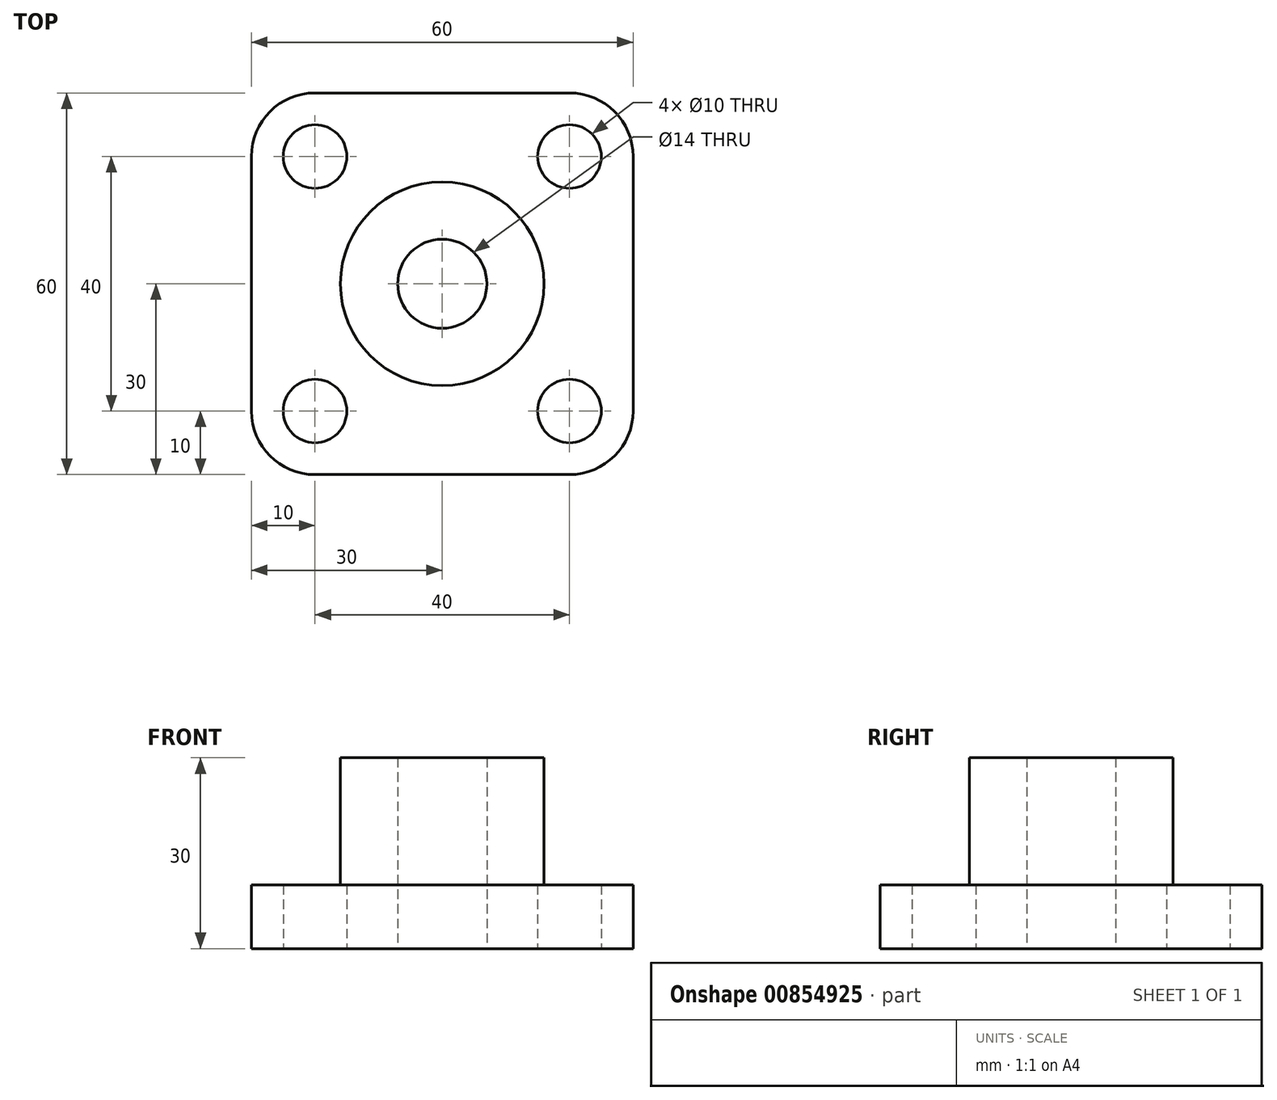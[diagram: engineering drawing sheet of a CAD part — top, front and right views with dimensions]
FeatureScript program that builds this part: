
annotation { "Feature Type Name" : "Feature", "Feature Type Description" : "" }
export const myFeature = defineFeature(function(context is Context, id is Id, definition is map)
    precondition{}
    {
        {
            var Q0;
            Q0=qCreatedBy(makeId("Front.planeOp"),FACE);
            var sketch = newSketch(context, id + "F0", { "sketchPlane" : qUnion([Q0])});
            skCircle(sketch, "E0", {"center": v(0, 0) * mm, "radius": 16 * mm});
            skLineSegment(sketch, "E1", {"start": v(0, 0) * mm, "end": v(-20, 0) * mm});
            skLineSegment(sketch, "E2", {"start": v(0, 0) * mm, "end": v(20, 0) * mm});
            skLineSegment(sketch, "E3", {"start": v(-20, 0) * mm, "end": v(-20, -20) * mm});
            skLineSegment(sketch, "E4", {"start": v(-20, 0) * mm, "end": v(-20, 20) * mm});
            skLineSegment(sketch, "E5", {"start": v(20, 0) * mm, "end": v(20, -20) * mm});
            skLineSegment(sketch, "E6", {"start": v(20, 0) * mm, "end": v(20, 20) * mm});
            skCircle(sketch, "E7", {"center": v(-20, 20) * mm, "radius": 5 * mm});
            skCircle(sketch, "E8", {"center": v(-20, -20) * mm, "radius": 5 * mm});
            skCircle(sketch, "E9", {"center": v(20, -20) * mm, "radius": 5 * mm});
            skCircle(sketch, "E10", {"center": v(20, 20) * mm, "radius": 5 * mm});
            skArc(sketch, "E11", {"start": v(-20, 30) * mm, "mid": v(-27.07, 27.07) * mm, "end": v(-30, 20) * mm});
            skArc(sketch, "E12", {"start": v(30, 20) * mm, "mid": v(27.07, 27.07) * mm, "end": v(20, 30) * mm});
            skArc(sketch, "E13", {"start": v(20, -30) * mm, "mid": v(27.07, -27.07) * mm, "end": v(30, -20) * mm});
            skArc(sketch, "E14", {"start": v(-30, -20) * mm, "mid": v(-27.07, -27.07) * mm, "end": v(-20, -30) * mm});
            skLineSegment(sketch, "E15", {"start": v(-20, -30) * mm, "end": v(20, -30) * mm});
            skLineSegment(sketch, "E16", {"start": v(30, 20) * mm, "end": v(30, -20) * mm});
            skLineSegment(sketch, "E17", {"start": v(-20, 30) * mm, "end": v(20, 30) * mm});
            skLineSegment(sketch, "E18", {"start": v(-30, 20) * mm, "end": v(-30, -20) * mm});
            skSolve(sketch);
        }
        {
            var Q0;
            {var subQ0=sQuery(id+"F0.wireOp",EDGE,"E18");Q0=makeQuery(id+"F0.imprint","IMPRINT",FACE,{"disambiguationData":[TD([[makeQuery(id+"F0.imprint","IMPRINT",EDGE,{"derivedFrom":subQ0}),1.0]])]});}
            var Q1;
            {var subQ5=sQuery(id+"F0.wireOp",EDGE,"E17");Q1=makeQuery(id+"F0.imprint","IMPRINT",FACE,{"disambiguationData":[TD([[makeQuery(id+"F0.imprint","IMPRINT",EDGE,{"derivedFrom":subQ5}),-1.0]])]});}
            var Q2;
            Q2=makeQuery(id+"F0.imprint","IMPRINT",FACE,{"disambiguationData":[TD([[makeQuery(id+"F0.imprint","IMPRINT",EDGE,{"derivedFrom":sQuery(id+"F0.wireOp",EDGE,"E7")}),-1.0]])]});
            var Q3;
            Q3=makeQuery(id+"F0.imprint","IMPRINT",FACE,{"disambiguationData":[TD([[makeQuery(id+"F0.imprint","IMPRINT",EDGE,{"derivedFrom":sQuery(id+"F0.wireOp",EDGE,"E10")}),-1.0]])]});
            var Q4;
            {var subQ0=sQuery(id+"F0.wireOp",EDGE,"E16");Q4=makeQuery(id+"F0.imprint","IMPRINT",FACE,{"disambiguationData":[TD([[makeQuery(id+"F0.imprint","IMPRINT",EDGE,{"derivedFrom":subQ0}),-1.0]])]});}
            var Q5;
            {var subQ9=sQuery(id+"F0.wireOp",EDGE,"E15");Q5=makeQuery(id+"F0.imprint","IMPRINT",FACE,{"disambiguationData":[TD([[makeQuery(id+"F0.imprint","IMPRINT",EDGE,{"derivedFrom":subQ9}),1.0]])]});}
            var Q6;
            Q6=makeQuery(id+"F0.imprint","IMPRINT",FACE,{"disambiguationData":[TD([[makeQuery(id+"F0.imprint","IMPRINT",EDGE,{"derivedFrom":sQuery(id+"F0.wireOp",EDGE,"E9")}),-1.0]])]});
            var Q7;
            Q7=makeQuery(id+"F0.imprint","IMPRINT",FACE,{"disambiguationData":[TD([[makeQuery(id+"F0.imprint","IMPRINT",EDGE,{"derivedFrom":sQuery(id+"F0.wireOp",EDGE,"E8")}),-1.0]])]});
            var Q8;
            {var subQ0=sQuery(id+"F0.wireOp",EDGE,"E1");var subQ1=sQuery(id+"F0.wireOp",EDGE,"E0");var subQ2=makeQuery(id+"F0.imprint","INTERSECT",VERTEX,{"derivedFrom":[subQ1,subQ0]});Q8=makeQuery(id+"F0.imprint","IMPRINT",FACE,{"disambiguationData":[TD([[makeQuery(id+"F0.imprint","IMPRINT",EDGE,{"disambiguationData":[TD([[subQ2,-1.0]])],"derivedFrom":subQ1}),1.0]])]});}
            var Q9;
            {var subQ0=sQuery(id+"F0.wireOp",EDGE,"E1");var subQ1=sQuery(id+"F0.wireOp",EDGE,"E0");var subQ2=makeQuery(id+"F0.imprint","INTERSECT",VERTEX,{"derivedFrom":[subQ1,subQ0]});Q9=makeQuery(id+"F0.imprint","IMPRINT",FACE,{"disambiguationData":[TD([[makeQuery(id+"F0.imprint","IMPRINT",EDGE,{"disambiguationData":[TD([[subQ2,1.0]])],"derivedFrom":subQ1}),1.0]])]});}
            extrude(context, id + "F1", {"entities" : qUnion([Q0, Q1, Q2, Q3, Q4, Q5, Q6, Q7, Q8, Q9]), "depth" : 10 * mm, "offsetDistance" : 25 * mm});
        }
        {
            var Q0;
            Q0=makeQuery(id+"F1.opExtrude","CAP_FACE",FACE,{"disambiguationData":[OSD([sQuery(id+"F0.wireOp",EDGE,"E7"),sQuery(id+"F0.wireOp",EDGE,"E8"),sQuery(id+"F0.wireOp",EDGE,"E9"),sQuery(id+"F0.wireOp",EDGE,"E10"),sQuery(id+"F0.wireOp",EDGE,"E11"),sQuery(id+"F0.wireOp",EDGE,"E12"),sQuery(id+"F0.wireOp",EDGE,"E13"),sQuery(id+"F0.wireOp",EDGE,"E14"),sQuery(id+"F0.wireOp",EDGE,"E15"),sQuery(id+"F0.wireOp",EDGE,"E16"),sQuery(id+"F0.wireOp",EDGE,"E17"),sQuery(id+"F0.wireOp",EDGE,"E18")])],"isStart":false});
            var sketch = newSketch(context, id + "F2", { "sketchPlane" : qUnion([Q0])});
            skCircle(sketch, "E19", {"center": v(0, 0) * mm, "radius": 16 * mm});
            skSolve(sketch);
        }
        {
            var Q0;
            Q0=makeQuery(id+"F2.imprint","IMPRINT",FACE,{"disambiguationData":[TD([[makeQuery(id+"F2.imprint","IMPRINT",EDGE,{"derivedFrom":sQuery(id+"F2.wireOp",EDGE,"E19")}),1.0]])]});
            extrude(context, id + "F3", {"entities" : qUnion([Q0]), "operationType" : NewBodyOperationType.ADD, "depth" : 20 * mm, "offsetDistance" : 25 * mm});
        }
        {
            var Q0;
            Q0=sQuery(id+"F0.wireOp",VERTEX,"E1.start");
            var Q1;
            Q1=makeQuery(id+"F1.opExtrude","SWEPT_BODY",BODY,{"disambiguationData":[OSD([sQuery(id+"F0.wireOp",EDGE,"E7"),sQuery(id+"F0.wireOp",EDGE,"E8"),sQuery(id+"F0.wireOp",EDGE,"E9"),sQuery(id+"F0.wireOp",EDGE,"E10"),sQuery(id+"F0.wireOp",EDGE,"E11"),sQuery(id+"F0.wireOp",EDGE,"E12"),sQuery(id+"F0.wireOp",EDGE,"E13"),sQuery(id+"F0.wireOp",EDGE,"E14"),sQuery(id+"F0.wireOp",EDGE,"E15"),sQuery(id+"F0.wireOp",EDGE,"E16"),sQuery(id+"F0.wireOp",EDGE,"E17"),sQuery(id+"F0.wireOp",EDGE,"E18")])]});
            hole(context, id + "F4", {"style" : HoleStyle.SIMPLE, "endStyle" : HoleEndStyle.BLIND, "oppositeDirection" : true, "standardTappedOrClearance" : lookupTablePath({ "standard" : "ISO", "engagement" : "75%", "pitch" : "2 mm", "size" : "M16", "type" : "Tapped" }), "standardBlindInLast" : lookupTablePath({ "standard" : "ISO", "engagement" : "75%", "pitch" : "2 mm", "size" : "M16", "type" : "Tapped" }), "holeDiameter" : 14 * mm, "majorDiameter" : 16 * mm, "showTappedDepth" : true, "holeDepth" : 31 * mm, "isTappedThrough" : true, "tappedDepth" : 25 * mm, "tapClearance" : 3, "locations" : qUnion([Q0]), "scope" : qUnion([Q1])});
        }
        {
            var Q0;
            Q0=makeQuery(id+"F1.opExtrude","SWEPT_BODY",BODY,{"disambiguationData":[OSD([sQuery(id+"F0.wireOp",EDGE,"E7"),sQuery(id+"F0.wireOp",EDGE,"E8"),sQuery(id+"F0.wireOp",EDGE,"E9"),sQuery(id+"F0.wireOp",EDGE,"E10"),sQuery(id+"F0.wireOp",EDGE,"E11"),sQuery(id+"F0.wireOp",EDGE,"E12"),sQuery(id+"F0.wireOp",EDGE,"E13"),sQuery(id+"F0.wireOp",EDGE,"E14"),sQuery(id+"F0.wireOp",EDGE,"E15"),sQuery(id+"F0.wireOp",EDGE,"E16"),sQuery(id+"F0.wireOp",EDGE,"E17"),sQuery(id+"F0.wireOp",EDGE,"E18")])]});
            var Q1;
            Q1=sQuery(id+"F0.wireOp",EDGE,"E2");
            transform(context, id + "F5", {"entities" : qUnion([Q0]), "transformType" : TransformType.ROTATION, "transformAxis" : qUnion([Q1]), "angle" : 90 * degree, "oppositeDirection" : true, "makeCopy" : false});
        }
    });
